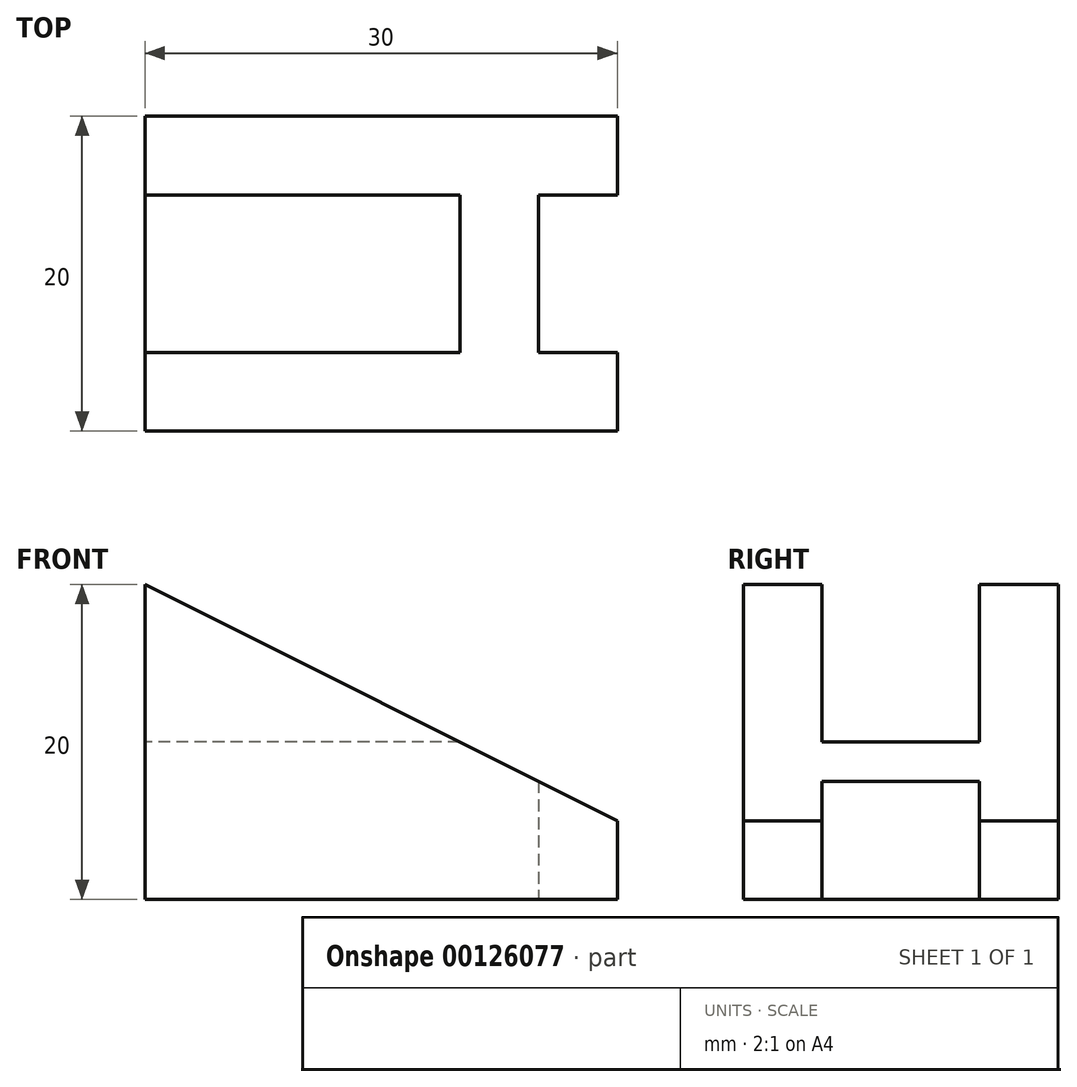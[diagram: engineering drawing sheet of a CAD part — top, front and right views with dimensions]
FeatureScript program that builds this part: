
annotation { "Feature Type Name" : "Feature", "Feature Type Description" : "" }
export const myFeature = defineFeature(function(context is Context, id is Id, definition is map)
    precondition{}
    {
        {
            var Q0;
            Q0=qCreatedBy(makeId("Front.planeOp"),FACE);
            var sketch = newSketch(context, id + "F0", { "sketchPlane" : qUnion([Q0])});
            skLineSegment(sketch, "E0", {"start": v(0, 0) * mm, "end": v(0, 20) * mm});
            skLineSegment(sketch, "E1", {"start": v(0, 20) * mm, "end": v(30, 5) * mm});
            skLineSegment(sketch, "E2", {"start": v(30, 5) * mm, "end": v(30, 0) * mm});
            skLineSegment(sketch, "E3", {"start": v(30, 0) * mm, "end": v(0, 0) * mm});
            skSolve(sketch);
        }
        {
            var Q0;
            Q0=makeQuery(id+"F0.imprint","IMPRINT",FACE,{"disambiguationData":[TD([[makeQuery(id+"F0.imprint","IMPRINT",EDGE,{"derivedFrom":sQuery(id+"F0.wireOp",EDGE,"E0")}),-1.0]])]});
            extrude(context, id + "F1", {"entities" : qUnion([Q0]), "oppositeDirection" : true, "depth" : 20 * mm});
        }
        {
            var Q0;
            Q0=makeQuery(id+"F1.opExtrude","SWEPT_FACE",FACE,{"disambiguationData":[OSD([sQuery(id+"F0.wireOp",EDGE,"E3")])]});
            var sketch = newSketch(context, id + "F2", { "sketchPlane" : qUnion([Q0])});
            skLineSegment(sketch, "E4.bottom", {"start": v(30, -5) * mm, "end": v(25, -5) * mm});
            skLineSegment(sketch, "E4.top", {"start": v(30, -15) * mm, "end": v(25, -15) * mm});
            skLineSegment(sketch, "E4.left", {"start": v(30, -5) * mm, "end": v(30, -15) * mm});
            skLineSegment(sketch, "E4.right", {"start": v(25, -5) * mm, "end": v(25, -15) * mm});
            skSolve(sketch);
        }
        {
            var Q0;
            Q0=makeQuery(id+"F2.imprint","IMPRINT",FACE,{"disambiguationData":[TD([[makeQuery(id+"F2.imprint","IMPRINT",EDGE,{"derivedFrom":sQuery(id+"F2.wireOp",EDGE,"E4.bottom")}),1.0]])]});
            extrude(context, id + "F3", {"entities" : qUnion([Q0]), "operationType" : NewBodyOperationType.REMOVE, "endBound" : BoundingType.THROUGH_ALL, "oppositeDirection" : true, "depth" : 25 * mm});
        }
        {
            var Q0;
            Q0=makeQuery(id+"F1.opExtrude","SWEPT_FACE",FACE,{"disambiguationData":[OSD([sQuery(id+"F0.wireOp",EDGE,"E0")])]});
            var sketch = newSketch(context, id + "F4", { "sketchPlane" : qUnion([Q0])});
            skLineSegment(sketch, "E5.bottom", {"start": v(-15, 20) * mm, "end": v(-5, 20) * mm});
            skLineSegment(sketch, "E5.top", {"start": v(-15, 10) * mm, "end": v(-5, 10) * mm});
            skLineSegment(sketch, "E5.left", {"start": v(-15, 20) * mm, "end": v(-15, 10) * mm});
            skLineSegment(sketch, "E5.right", {"start": v(-5, 20) * mm, "end": v(-5, 10) * mm});
            skSolve(sketch);
        }
        {
            var Q0;
            Q0=makeQuery(id+"F4.imprint","IMPRINT",FACE,{"disambiguationData":[TD([[makeQuery(id+"F4.imprint","IMPRINT",EDGE,{"derivedFrom":sQuery(id+"F4.wireOp",EDGE,"E5.bottom")}),-1.0]])]});
            extrude(context, id + "F5", {"entities" : qUnion([Q0]), "operationType" : NewBodyOperationType.REMOVE, "endBound" : BoundingType.THROUGH_ALL, "oppositeDirection" : true, "depth" : 25 * mm});
        }
    });
